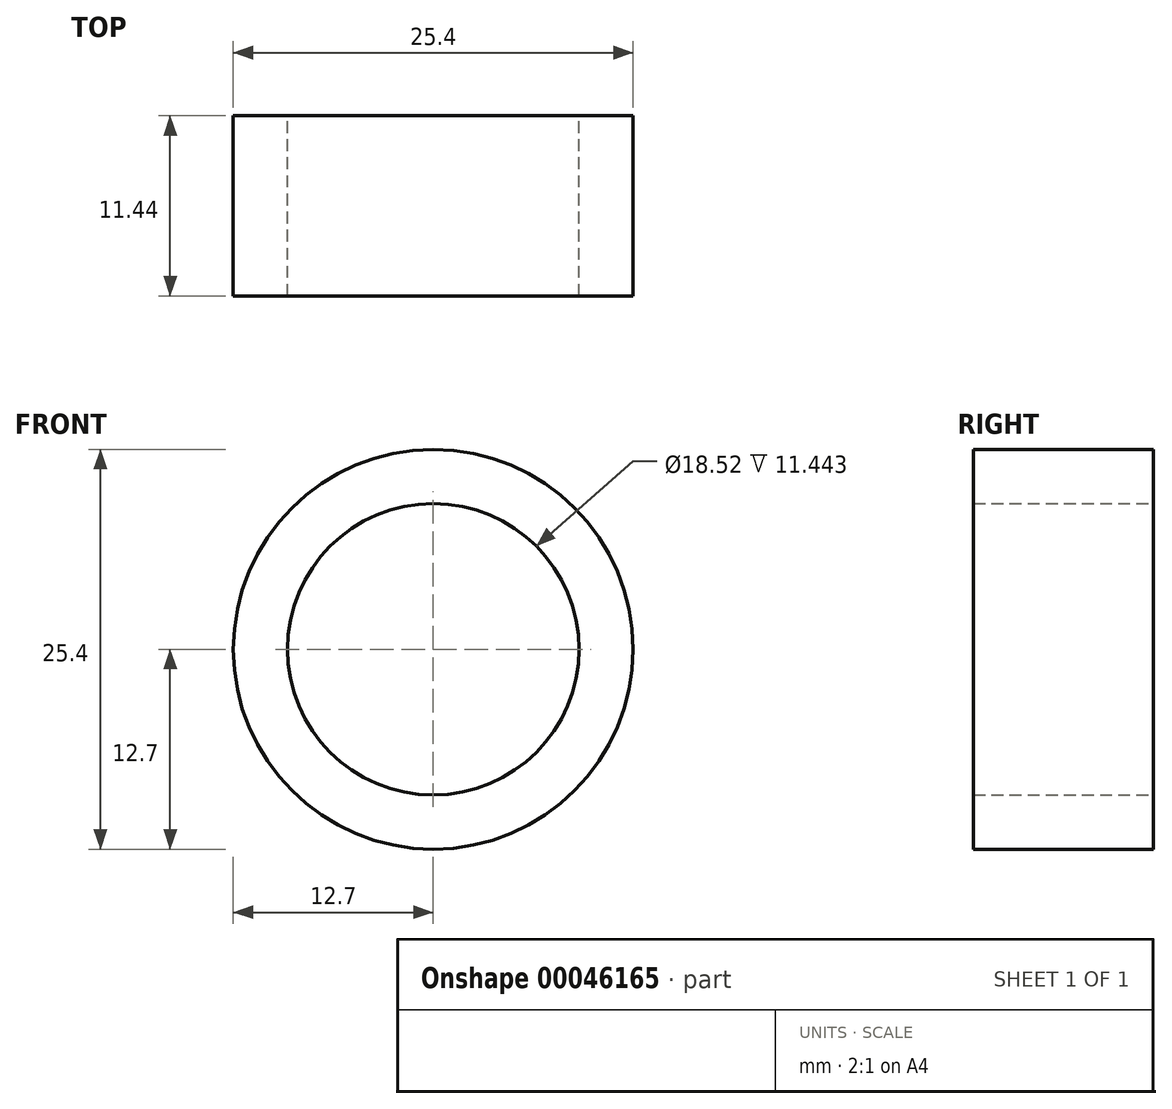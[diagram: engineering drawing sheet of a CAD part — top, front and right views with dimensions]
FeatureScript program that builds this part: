
annotation { "Feature Type Name" : "Feature", "Feature Type Description" : "" }
export const myFeature = defineFeature(function(context is Context, id is Id, definition is map)
    precondition{}
    {
        {
            var Q0;
            Q0=qCreatedBy(makeId("Front.planeOp"),FACE);
            var sketch = newSketch(context, id + "F0", { "sketchPlane" : qUnion([Q0])});
            skCircle(sketch, "E0", {"center": v(0, 0) * mm, "radius": 12.7 * mm});
            skCircle(sketch, "E1", {"center": v(0, 0) * mm, "radius": 9.26 * mm});
            skSolve(sketch);
        }
        {
            var Q0;
            Q0 = qSketchRegion(id + "F0", true);
            extrude(context, id + "F1", {"entities" : qUnion([Q0]), "depth" : 11.44 * mm});
        }
    });
